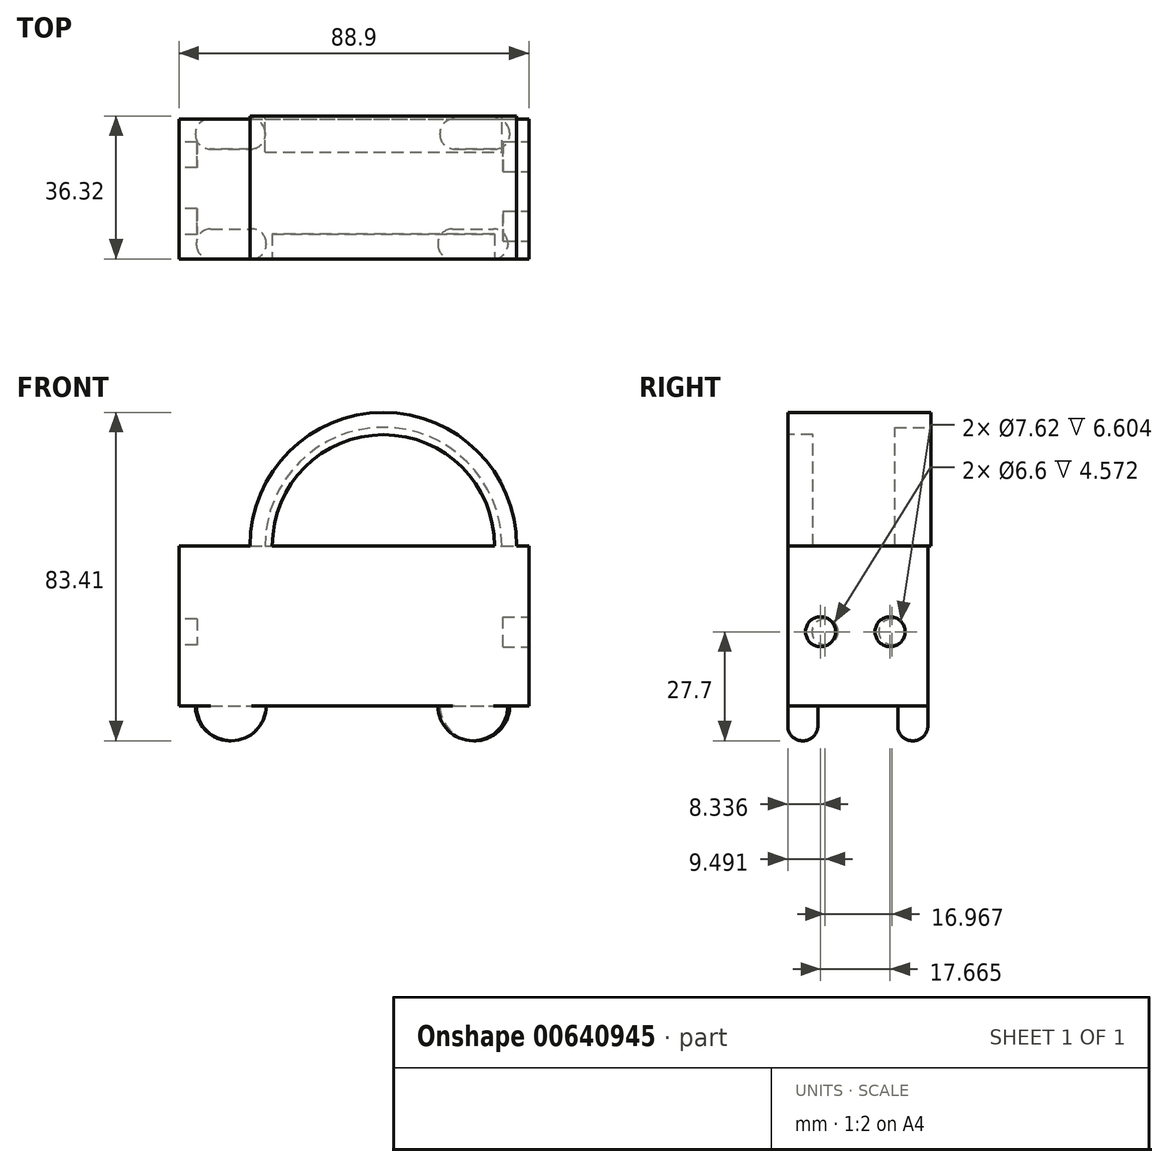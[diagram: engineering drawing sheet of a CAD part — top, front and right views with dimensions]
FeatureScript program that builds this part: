
annotation { "Feature Type Name" : "Feature", "Feature Type Description" : "" }
export const myFeature = defineFeature(function(context is Context, id is Id, definition is map)
    precondition{}
    {
        {
            var Q0;
            Q0=qCreatedBy(makeId("Front.planeOp"),FACE);
            var sketch = newSketch(context, id + "F0", { "sketchPlane" : qUnion([Q0])});
            skLineSegment(sketch, "E0.bottom", {"start": v(-42.76, 21.83) * mm, "end": v(46.14, 21.83) * mm});
            skLineSegment(sketch, "E0.top", {"start": v(-42.76, -18.8) * mm, "end": v(46.14, -18.8) * mm});
            skLineSegment(sketch, "E0.left", {"start": v(-42.76, 21.83) * mm, "end": v(-42.76, -18.8) * mm});
            skLineSegment(sketch, "E0.right", {"start": v(46.14, 21.83) * mm, "end": v(46.14, -18.8) * mm});
            skSolve(sketch);
        }
        {
            var Q0;
            Q0 = qSketchRegion(id + "F0", true);
            extrude(context, id + "F1", {"entities" : qUnion([Q0]), "depth" : 35.56 * mm, "offsetDistance" : 25.4 * mm});
        }
        {
            var Q0;
            Q0=makeQuery(id+"F1.opExtrude","CAP_FACE",FACE,{"disambiguationData":[OSD([sQuery(id+"F0.wireOp",EDGE,"E0.bottom"),sQuery(id+"F0.wireOp",EDGE,"E0.top"),sQuery(id+"F0.wireOp",EDGE,"E0.left"),sQuery(id+"F0.wireOp",EDGE,"E0.right")])],"isStart":false});
            var sketch = newSketch(context, id + "F2", { "sketchPlane" : qUnion([Q0])});
            skArc(sketch, "E1", {"start": v(-38.36, -18.8) * mm, "mid": v(-29.47, -27.7) * mm, "end": v(-20.58, -18.8) * mm});
            skArc(sketch, "E2", {"start": v(23.02, -18.8) * mm, "mid": v(31.9, -27.7) * mm, "end": v(40.8, -18.8) * mm});
            skLineSegment(sketch, "E3", {"start": v(-20.58, -18.8) * mm, "end": v(-38.36, -18.8) * mm});
            skLineSegment(sketch, "E4", {"start": v(40.8, -18.8) * mm, "end": v(23.02, -18.8) * mm});
            skSolve(sketch);
        }
        {
            var Q0;
            Q0 = qSketchRegion(id + "F2", true);
            extrude(context, id + "F3", {"entities" : qUnion([Q0]), "operationType" : NewBodyOperationType.ADD, "oppositeDirection" : true, "depth" : 7.62 * mm, "offsetDistance" : 25.4 * mm});
        }
        {
            var Q0;
            Q0=makeQuery(id+"F1.opExtrude","CAP_FACE",FACE,{"disambiguationData":[OSD([sQuery(id+"F0.wireOp",EDGE,"E0.bottom"),sQuery(id+"F0.wireOp",EDGE,"E0.top"),sQuery(id+"F0.wireOp",EDGE,"E0.left"),sQuery(id+"F0.wireOp",EDGE,"E0.right")])],"isStart":true});
            var sketch = newSketch(context, id + "F4", { "sketchPlane" : qUnion([Q0])});
            skArc(sketch, "E5", {"start": v(-41.28, -18.8) * mm, "mid": v(-32.4, -27.7) * mm, "end": v(-23.5, -18.8) * mm});
            skArc(sketch, "E6", {"start": v(20.82, -18.8) * mm, "mid": v(29.71, -27.7) * mm, "end": v(38.6, -18.8) * mm});
            skLineSegment(sketch, "E7", {"start": v(-23.5, -18.8) * mm, "end": v(-41.28, -18.8) * mm});
            skLineSegment(sketch, "E8", {"start": v(38.6, -18.8) * mm, "end": v(20.82, -18.8) * mm});
            skSolve(sketch);
        }
        {
            var Q0;
            Q0 = qSketchRegion(id + "F4", true);
            extrude(context, id + "F5", {"entities" : qUnion([Q0]), "operationType" : NewBodyOperationType.ADD, "oppositeDirection" : true, "depth" : 7.62 * mm, "offsetDistance" : 25.4 * mm});
        }
        {
            var Q0;
            Q0=makeQuery(id+"F3.boolean.opBoolean","MERGE",FACE,{"derivedFrom":[makeQuery(id+"F1.opExtrude","CAP_FACE",FACE,{"disambiguationData":[OSD([sQuery(id+"F0.wireOp",EDGE,"E0.bottom"),sQuery(id+"F0.wireOp",EDGE,"E0.top"),sQuery(id+"F0.wireOp",EDGE,"E0.left"),sQuery(id+"F0.wireOp",EDGE,"E0.right")])],"isStart":false}),makeQuery(id+"F3.opExtrude","CAP_FACE",FACE,{"disambiguationData":[OSD([sQuery(id+"F2.wireOp",EDGE,"E1"),sQuery(id+"F2.wireOp",EDGE,"E3")])],"isStart":true}),makeQuery(id+"F3.opExtrude","CAP_FACE",FACE,{"disambiguationData":[OSD([sQuery(id+"F2.wireOp",EDGE,"E2"),sQuery(id+"F2.wireOp",EDGE,"E4")])],"isStart":true})]});
            var sketch = newSketch(context, id + "F6", { "sketchPlane" : qUnion([Q0])});
            skArc(sketch, "E9", {"start": v(43.05, 21.83) * mm, "mid": v(9.17, 55.7) * mm, "end": v(-24.7, 21.83) * mm});
            skLineSegment(sketch, "E10", {"start": v(43.05, 21.83) * mm, "end": v(-24.7, 21.83) * mm});
            skSolve(sketch);
        }
        {
            var Q0;
            Q0 = qSketchRegion(id + "F6", true);
            extrude(context, id + "F7", {"entities" : qUnion([Q0]), "operationType" : NewBodyOperationType.ADD, "oppositeDirection" : true, "depth" : 36.32 * mm, "offsetDistance" : 25.4 * mm});
        }
        {
            var Q0;
            Q0=makeQuery(id+"F7.boolean.opBoolean","MERGE",FACE,{"derivedFrom":[makeQuery(id+"F3.boolean.opBoolean","MERGE",FACE,{"derivedFrom":[makeQuery(id+"F1.opExtrude","CAP_FACE",FACE,{"disambiguationData":[OSD([sQuery(id+"F0.wireOp",EDGE,"E0.bottom"),sQuery(id+"F0.wireOp",EDGE,"E0.top"),sQuery(id+"F0.wireOp",EDGE,"E0.left"),sQuery(id+"F0.wireOp",EDGE,"E0.right")])],"isStart":false}),makeQuery(id+"F3.opExtrude","CAP_FACE",FACE,{"disambiguationData":[OSD([sQuery(id+"F2.wireOp",EDGE,"E1"),sQuery(id+"F2.wireOp",EDGE,"E3")])],"isStart":true}),makeQuery(id+"F3.opExtrude","CAP_FACE",FACE,{"disambiguationData":[OSD([sQuery(id+"F2.wireOp",EDGE,"E2"),sQuery(id+"F2.wireOp",EDGE,"E4")])],"isStart":true})]}),makeQuery(id+"F7.opExtrude","CAP_FACE",FACE,{"disambiguationData":[OSD([sQuery(id+"F6.wireOp",EDGE,"E9"),sQuery(id+"F6.wireOp",EDGE,"E10")])],"isStart":true})]});
            var sketch = newSketch(context, id + "F8", { "sketchPlane" : qUnion([Q0])});
            skArc(sketch, "E11", {"start": v(34.6, 24.2) * mm, "mid": v(7.85, 50.96) * mm, "end": v(-18.9, 24.2) * mm});
            skLineSegment(sketch, "E12", {"start": v(-18.9, 24.2) * mm, "end": v(34.6, 24.2) * mm});
            skSolve(sketch);
        }
        {
            var Q0;
            Q0 = qSketchRegion(id + "F8", true);
            extrude(context, id + "F9", {"entities" : qUnion([Q0]), "operationType" : NewBodyOperationType.ADD, "oppositeDirection" : true, "depth" : 9.9 * mm, "offsetDistance" : 25.4 * mm});
        }
        {
            var Q0;
            Q0=makeQuery(id+"F7.boolean.opBoolean","MERGE",FACE,{"derivedFrom":[makeQuery(id+"F3.boolean.opBoolean","MERGE",FACE,{"derivedFrom":[makeQuery(id+"F1.opExtrude","CAP_FACE",FACE,{"disambiguationData":[OSD([sQuery(id+"F0.wireOp",EDGE,"E0.bottom"),sQuery(id+"F0.wireOp",EDGE,"E0.top"),sQuery(id+"F0.wireOp",EDGE,"E0.left"),sQuery(id+"F0.wireOp",EDGE,"E0.right")])],"isStart":false}),makeQuery(id+"F3.opExtrude","CAP_FACE",FACE,{"disambiguationData":[OSD([sQuery(id+"F2.wireOp",EDGE,"E1"),sQuery(id+"F2.wireOp",EDGE,"E3")])],"isStart":true}),makeQuery(id+"F3.opExtrude","CAP_FACE",FACE,{"disambiguationData":[OSD([sQuery(id+"F2.wireOp",EDGE,"E2"),sQuery(id+"F2.wireOp",EDGE,"E4")])],"isStart":true})]}),makeQuery(id+"F7.opExtrude","CAP_FACE",FACE,{"disambiguationData":[OSD([sQuery(id+"F6.wireOp",EDGE,"E9"),sQuery(id+"F6.wireOp",EDGE,"E10")])],"isStart":true})]});
            var sketch = newSketch(context, id + "F10", { "sketchPlane" : qUnion([Q0])});
            skArc(sketch, "E13", {"start": v(37.4, 21.83) * mm, "mid": v(9.17, 50.06) * mm, "end": v(-19.05, 21.83) * mm});
            skLineSegment(sketch, "E14", {"start": v(-19.05, 21.83) * mm, "end": v(37.4, 21.83) * mm});
            skSolve(sketch);
        }
        {
            var Q0;
            Q0 = qSketchRegion(id + "F10", true);
            extrude(context, id + "F11", {"entities" : qUnion([Q0]), "operationType" : NewBodyOperationType.REMOVE, "oppositeDirection" : true, "depth" : 6.35 * mm, "offsetDistance" : 25.4 * mm});
        }
        {
            var Q0;
            Q0=makeQuery(id+"F7.opExtrude","CAP_FACE",FACE,{"disambiguationData":[OSD([sQuery(id+"F6.wireOp",EDGE,"E9"),sQuery(id+"F6.wireOp",EDGE,"E10")])],"isStart":false});
            var sketch = newSketch(context, id + "F12", { "sketchPlane" : qUnion([Q0])});
            skArc(sketch, "E15", {"start": v(20.91, 21.83) * mm, "mid": v(-9.17, 51.92) * mm, "end": v(-39.26, 21.83) * mm});
            skLineSegment(sketch, "E16", {"start": v(-39.26, 21.83) * mm, "end": v(20.91, 21.83) * mm});
            skSolve(sketch);
        }
        {
            var Q0;
            Q0 = qSketchRegion(id + "F12", true);
            extrude(context, id + "F13", {"entities" : qUnion([Q0]), "operationType" : NewBodyOperationType.REMOVE, "oppositeDirection" : true, "depth" : 9.14 * mm, "offsetDistance" : 25.4 * mm});
        }
        {
            var Q0;
            Q0=makeQuery(id+"F1.opExtrude","SWEPT_FACE",FACE,{"disambiguationData":[OSD([sQuery(id+"F0.wireOp",EDGE,"E0.right")])]});
            var sketch = newSketch(context, id + "F14", { "sketchPlane" : qUnion([Q0])});
            skCircle(sketch, "E17", {"center": v(-27.22, 0) * mm, "radius": 3.81 * mm});
            skCircle(sketch, "E18", {"center": v(-9.56, 0) * mm, "radius": 3.81 * mm});
            skSolve(sketch);
        }
        {
            var Q0;
            Q0 = qSketchRegion(id + "F14", true);
            extrude(context, id + "F15", {"entities" : qUnion([Q0]), "operationType" : NewBodyOperationType.REMOVE, "oppositeDirection" : true, "depth" : 6.6 * mm, "offsetDistance" : 25.4 * mm});
        }
        {
            var Q0;
            Q0=makeQuery(id+"F1.opExtrude","SWEPT_FACE",FACE,{"disambiguationData":[OSD([sQuery(id+"F0.wireOp",EDGE,"E0.left")])]});
            var sketch = newSketch(context, id + "F16", { "sketchPlane" : qUnion([Q0])});
            skCircle(sketch, "E19", {"center": v(9.1, 0) * mm, "radius": 3.3 * mm});
            skCircle(sketch, "E20", {"center": v(26.07, 0) * mm, "radius": 3.3 * mm});
            skSolve(sketch);
        }
        {
            var Q0;
            Q0 = qSketchRegion(id + "F16", true);
            extrude(context, id + "F17", {"entities" : qUnion([Q0]), "operationType" : NewBodyOperationType.REMOVE, "oppositeDirection" : true, "depth" : 4.57 * mm, "offsetDistance" : 25.4 * mm});
        }
        {
            var Q0;
            Q0=makeQuery(id+"F3.opExtrude","CAP_EDGE",EDGE,{"disambiguationData":[OSD([sQuery(id+"F2.wireOp",EDGE,"E1")])],"isStart":true});
            var Q1;
            Q1=makeQuery(id+"F5.opExtrude","CAP_EDGE",EDGE,{"disambiguationData":[OSD([sQuery(id+"F4.wireOp",EDGE,"E6")])],"isStart":false});
            var Q2;
            Q2=makeQuery(id+"F5.opExtrude","CAP_EDGE",EDGE,{"disambiguationData":[OSD([sQuery(id+"F4.wireOp",EDGE,"E6")])],"isStart":true});
            var Q3;
            Q3=makeQuery(id+"F5.opExtrude","CAP_EDGE",EDGE,{"disambiguationData":[OSD([sQuery(id+"F4.wireOp",EDGE,"E5")])],"isStart":true});
            var Q4;
            Q4=makeQuery(id+"F3.opExtrude","CAP_EDGE",EDGE,{"disambiguationData":[OSD([sQuery(id+"F2.wireOp",EDGE,"E2")])],"isStart":false});
            var Q5;
            Q5=makeQuery(id+"F5.opExtrude","CAP_EDGE",EDGE,{"disambiguationData":[OSD([sQuery(id+"F4.wireOp",EDGE,"E5")])],"isStart":false});
            var Q6;
            Q6=makeQuery(id+"F3.opExtrude","CAP_EDGE",EDGE,{"disambiguationData":[OSD([sQuery(id+"F2.wireOp",EDGE,"E1")])],"isStart":false});
            var Q7;
            Q7=makeQuery(id+"F3.opExtrude","CAP_EDGE",EDGE,{"disambiguationData":[OSD([sQuery(id+"F2.wireOp",EDGE,"E2")])],"isStart":true});
            fillet(context, id + "F18", {"entities" : qUnion([Q0, Q1, Q2, Q3, Q4, Q5, Q6, Q7]), "radius" : 3.68 * mm, "tangentPropagation" : true, "allowEdgeOverflow" : false});
        }
    });
